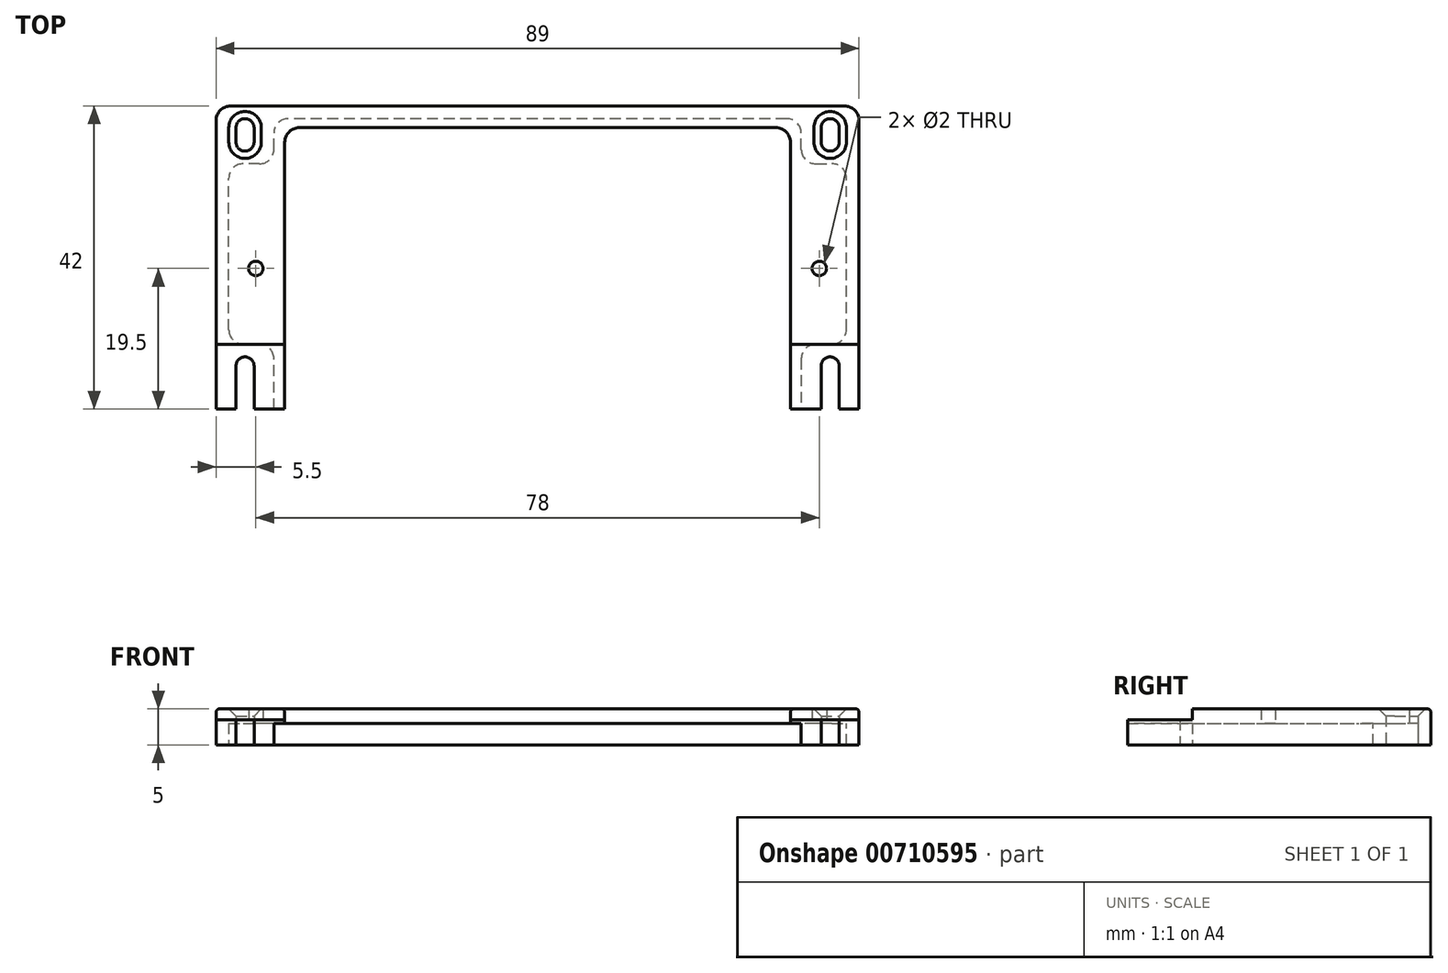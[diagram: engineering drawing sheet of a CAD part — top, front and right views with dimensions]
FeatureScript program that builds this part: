
annotation { "Feature Type Name" : "Feature", "Feature Type Description" : "" }
export const myFeature = defineFeature(function(context is Context, id is Id, definition is map)
    precondition{}
    {
        {
            var Q0;
            Q0=qCreatedBy(makeId("Top.planeOp"),FACE);
            var sketch = newSketch(context, id + "F0", { "sketchPlane" : qUnion([Q0])});
            skLineSegment(sketch, "E0.bottom", {"start": v(44.5, -22.5) * mm, "end": v(-44.5, -22.5) * mm});
            skLineSegment(sketch, "E0.top", {"start": v(44.5, 22.5) * mm, "end": v(-44.5, 22.5) * mm});
            skLineSegment(sketch, "E0.left", {"start": v(44.5, -22.5) * mm, "end": v(44.5, 22.5) * mm});
            skLineSegment(sketch, "E0.right", {"start": v(-44.5, -22.5) * mm, "end": v(-44.5, 22.5) * mm});
            skPoint(sketch, "E0.middle", {"position": v(0, 0) * mm});
            skSolve(sketch);
        }
        {
            var Q0;
            Q0=qSketchRegion(id+"F0",true);
            extrude(context, id + "F1", {"entities" : qUnion([Q0]), "depth" : 5 * mm, "offsetDistance" : 25 * mm});
        }
        {
            var Q0;
            Q0=qCreatedBy(makeId("Top.planeOp"),FACE);
            var sketch = newSketch(context, id + "F2", { "sketchPlane" : qUnion([Q0])});
            skLineSegment(sketch, "E1.bottom", {"start": v(35, -19.5) * mm, "end": v(-35, -19.5) * mm});
            skLineSegment(sketch, "E1.top", {"start": v(35, 19.5) * mm, "end": v(-35, 19.5) * mm});
            skLineSegment(sketch, "E1.left", {"start": v(35, -19.5) * mm, "end": v(35, 19.5) * mm});
            skLineSegment(sketch, "E1.right", {"start": v(-35, -19.5) * mm, "end": v(-35, 19.5) * mm});
            skPoint(sketch, "E1.middle", {"position": v(0, 0) * mm});
            skSolve(sketch);
        }
        {
            var Q0;
            Q0=qSketchRegion(id+"F2",true);
            extrude(context, id + "F3", {"entities" : qUnion([Q0]), "operationType" : NewBodyOperationType.REMOVE, "depth" : 25 * mm, "offsetDistance" : 25 * mm});
        }
        {
            var Q0;
            Q0=qCreatedBy(makeId("Top.planeOp"),FACE);
            var sketch = newSketch(context, id + "F4", { "sketchPlane" : qUnion([Q0])});
            skLineSegment(sketch, "E2.bottom", {"start": v(42.75, -20.75) * mm, "end": v(-42.75, -20.75) * mm});
            skLineSegment(sketch, "E2.top", {"start": v(42.75, 20.75) * mm, "end": v(-42.75, 20.75) * mm});
            skLineSegment(sketch, "E2.left", {"start": v(42.75, -20.75) * mm, "end": v(42.75, 20.75) * mm});
            skLineSegment(sketch, "E2.right", {"start": v(-42.75, -20.75) * mm, "end": v(-42.75, 20.75) * mm});
            skPoint(sketch, "E2.middle", {"position": v(0, 0) * mm});
            skSolve(sketch);
        }
        {
            var Q0;
            Q0=qSketchRegion(id+"F4",true);
            extrude(context, id + "F5", {"entities" : qUnion([Q0]), "operationType" : NewBodyOperationType.REMOVE, "depth" : 3 * mm, "offsetDistance" : 25 * mm});
        }
        {
            var Q0;
            Q0=qCreatedBy(makeId("Top.planeOp"),FACE);
            var sketch = newSketch(context, id + "F6", { "sketchPlane" : qUnion([Q0])});
            skLineSegment(sketch, "E3.bottom", {"start": v(-36.5, 14.5) * mm, "end": v(-44.5, 14.5) * mm});
            skLineSegment(sketch, "E3.top", {"start": v(-36.5, 22.5) * mm, "end": v(-44.5, 22.5) * mm});
            skLineSegment(sketch, "E3.left", {"start": v(-36.5, 14.5) * mm, "end": v(-36.5, 22.5) * mm});
            skLineSegment(sketch, "E3.right", {"start": v(-44.5, 14.5) * mm, "end": v(-44.5, 22.5) * mm});
            skPoint(sketch, "E3.middle", {"position": v(-40.5, 18.5) * mm});
            skLineSegment(sketch, "E4.bottom", {"start": v(-44.5, -22.5) * mm, "end": v(-36.5, -22.5) * mm});
            skLineSegment(sketch, "E4.top", {"start": v(-44.5, -10.5) * mm, "end": v(-36.5, -10.5) * mm});
            skLineSegment(sketch, "E4.left", {"start": v(-44.5, -22.5) * mm, "end": v(-44.5, -10.5) * mm});
            skLineSegment(sketch, "E4.right", {"start": v(-36.5, -22.5) * mm, "end": v(-36.5, -10.5) * mm});
            skPoint(sketch, "E4.middle", {"position": v(-40.5, -16.5) * mm});
            skLineSegment(sketch, "E5.bottom", {"start": v(36.5, 14.5) * mm, "end": v(44.5, 14.5) * mm});
            skLineSegment(sketch, "E5.top", {"start": v(36.5, 22.5) * mm, "end": v(44.5, 22.5) * mm});
            skLineSegment(sketch, "E5.left", {"start": v(36.5, 14.5) * mm, "end": v(36.5, 22.5) * mm});
            skLineSegment(sketch, "E5.right", {"start": v(44.5, 14.5) * mm, "end": v(44.5, 22.5) * mm});
            skPoint(sketch, "E5.middle", {"position": v(40.5, 18.5) * mm});
            skLineSegment(sketch, "E6.bottom", {"start": v(44.5, -10.5) * mm, "end": v(36.5, -10.5) * mm});
            skLineSegment(sketch, "E6.top", {"start": v(44.5, -22.5) * mm, "end": v(36.5, -22.5) * mm});
            skLineSegment(sketch, "E6.left", {"start": v(44.5, -10.5) * mm, "end": v(44.5, -22.5) * mm});
            skLineSegment(sketch, "E6.right", {"start": v(36.5, -10.5) * mm, "end": v(36.5, -22.5) * mm});
            skSolve(sketch);
        }
        {
            var Q0;
            Q0=qSketchRegion(id+"F6",true);
            extrude(context, id + "F7", {"entities" : qUnion([Q0]), "operationType" : NewBodyOperationType.ADD, "depth" : 3 * mm, "offsetDistance" : 25 * mm});
        }
        {
            var Q0;
            Q0=qCreatedBy(makeId("Top.planeOp"),FACE);
            var sketch = newSketch(context, id + "F8", { "sketchPlane" : qUnion([Q0])});
            skCircle(sketch, "E7", {"center": v(40.5, -13.5) * mm, "radius": 1.25 * mm});
            skCircle(sketch, "E8", {"center": v(40.5, 19.5) * mm, "radius": 1.25 * mm});
            skCircle(sketch, "E9", {"center": v(-40.5, -13.5) * mm, "radius": 1.25 * mm});
            skCircle(sketch, "E10", {"center": v(-40.5, 19.5) * mm, "radius": 1.25 * mm});
            skCircle(sketch, "E11", {"center": v(-39, 0) * mm, "radius": 1 * mm});
            skCircle(sketch, "E12", {"center": v(39, 0) * mm, "radius": 1 * mm});
            skCircle(sketch, "E13.1.0.0", {"center": v(-40.5, 17.5) * mm, "radius": 1.25 * mm});
            skLineSegment(sketch, "E13.direction1", {"start": v(-40.5, 19.5) * mm, "end": v(-40.5, 17.5) * mm, "construction": true});
            skCircle(sketch, "E14.1.0.0", {"center": v(40.5, 17.5) * mm, "radius": 1.25 * mm});
            skLineSegment(sketch, "E14.direction1", {"start": v(40.5, 19.5) * mm, "end": v(40.5, 17.5) * mm, "construction": true});
            skLineSegment(sketch, "E15.bottom", {"start": v(-41.75, -13.5) * mm, "end": v(-39.25, -13.5) * mm});
            skLineSegment(sketch, "E15.top", {"start": v(-41.75, -23.5) * mm, "end": v(-39.25, -23.5) * mm});
            skLineSegment(sketch, "E15.left", {"start": v(-41.75, -13.5) * mm, "end": v(-41.75, -23.5) * mm});
            skLineSegment(sketch, "E15.right", {"start": v(-39.25, -13.5) * mm, "end": v(-39.25, -23.5) * mm});
            skLineSegment(sketch, "E16.bottom", {"start": v(39.25, -13.5) * mm, "end": v(41.75, -13.5) * mm});
            skLineSegment(sketch, "E16.top", {"start": v(39.25, -23.5) * mm, "end": v(41.75, -23.5) * mm});
            skLineSegment(sketch, "E16.left", {"start": v(39.25, -13.5) * mm, "end": v(39.25, -23.5) * mm});
            skLineSegment(sketch, "E16.right", {"start": v(41.75, -13.5) * mm, "end": v(41.75, -23.5) * mm});
            skSolve(sketch);
        }
        {
            var Q0;
            Q0=qSketchRegion(id+"F8",true);
            extrude(context, id + "F9", {"entities" : qUnion([Q0]), "operationType" : NewBodyOperationType.REMOVE, "depth" : 25 * mm, "offsetDistance" : 25 * mm});
        }
        {
            var Q0;
            Q0 = qSketchRegion(id + "F8", true);
            extrude(context, id + "F10", {"entities" : qUnion([Q0]), "operationType" : NewBodyOperationType.REMOVE, "depth" : 25 * mm, "offsetDistance" : 25 * mm});
        }
        {
            var Q0;
            Q0=makeQuery(id+"F7.boolean.opBoolean","MERGE",FACE,{"derivedFrom":[makeQuery(id+"F1.opExtrude","CAP_FACE",FACE,{"disambiguationData":[OSD([sQuery(id+"F0.wireOp",EDGE,"E0.bottom"),sQuery(id+"F0.wireOp",EDGE,"E0.top"),sQuery(id+"F0.wireOp",EDGE,"E0.left"),sQuery(id+"F0.wireOp",EDGE,"E0.right")])],"isStart":true}),makeQuery(id+"F7.opExtrude","CAP_FACE",FACE,{"disambiguationData":[OSD([sQuery(id+"F6.wireOp",EDGE,"E3.bottom"),sQuery(id+"F6.wireOp",EDGE,"E3.top"),sQuery(id+"F6.wireOp",EDGE,"E3.left"),sQuery(id+"F6.wireOp",EDGE,"E3.right")])],"isStart":true}),makeQuery(id+"F7.opExtrude","CAP_FACE",FACE,{"disambiguationData":[OSD([sQuery(id+"F6.wireOp",EDGE,"E4.bottom"),sQuery(id+"F6.wireOp",EDGE,"E4.top"),sQuery(id+"F6.wireOp",EDGE,"E4.left"),sQuery(id+"F6.wireOp",EDGE,"E4.right")])],"isStart":true}),makeQuery(id+"F7.opExtrude","CAP_FACE",FACE,{"disambiguationData":[OSD([sQuery(id+"F6.wireOp",EDGE,"E5.bottom"),sQuery(id+"F6.wireOp",EDGE,"E5.top"),sQuery(id+"F6.wireOp",EDGE,"E5.left"),sQuery(id+"F6.wireOp",EDGE,"E5.right")])],"isStart":true}),makeQuery(id+"F7.opExtrude","CAP_FACE",FACE,{"disambiguationData":[OSD([sQuery(id+"F6.wireOp",EDGE,"E6.bottom"),sQuery(id+"F6.wireOp",EDGE,"E6.top"),sQuery(id+"F6.wireOp",EDGE,"E6.left"),sQuery(id+"F6.wireOp",EDGE,"E6.right")])],"isStart":true})]});
            var sketch = newSketch(context, id + "F11", { "sketchPlane" : qUnion([Q0])});
            skLineSegment(sketch, "E17.bottom", {"start": v(-41.75, -19.5) * mm, "end": v(-39.25, -19.5) * mm});
            skLineSegment(sketch, "E17.top", {"start": v(-41.75, -17.5) * mm, "end": v(-39.25, -17.5) * mm});
            skLineSegment(sketch, "E17.left", {"start": v(-41.75, -19.5) * mm, "end": v(-41.75, -17.5) * mm});
            skLineSegment(sketch, "E17.right", {"start": v(-39.25, -19.5) * mm, "end": v(-39.25, -17.5) * mm});
            skLineSegment(sketch, "E18.bottom", {"start": v(39.25, -19.5) * mm, "end": v(41.75, -19.5) * mm});
            skLineSegment(sketch, "E18.top", {"start": v(39.25, -17.5) * mm, "end": v(41.75, -17.5) * mm});
            skLineSegment(sketch, "E18.left", {"start": v(39.25, -19.5) * mm, "end": v(39.25, -17.5) * mm});
            skLineSegment(sketch, "E18.right", {"start": v(41.75, -19.5) * mm, "end": v(41.75, -17.5) * mm});
            skSolve(sketch);
        }
        {
            var Q0;
            Q0 = qSketchRegion(id + "F11", true);
            extrude(context, id + "F12", {"entities" : qUnion([Q0]), "operationType" : NewBodyOperationType.REMOVE, "oppositeDirection" : true, "depth" : 25 * mm, "offsetDistance" : 25 * mm});
        }
        {
            var Q0;
            Q0=makeQuery(id+"F1.opExtrude","CAP_FACE",FACE,{"disambiguationData":[OSD([sQuery(id+"F0.wireOp",EDGE,"E0.bottom"),sQuery(id+"F0.wireOp",EDGE,"E0.top"),sQuery(id+"F0.wireOp",EDGE,"E0.left"),sQuery(id+"F0.wireOp",EDGE,"E0.right")])],"isStart":false});
            var sketch = newSketch(context, id + "F13", { "sketchPlane" : qUnion([Q0])});
            skLineSegment(sketch, "E19.bottom", {"start": v(44.5, -22.5) * mm, "end": v(-44.5, -22.5) * mm});
            skLineSegment(sketch, "E19.top", {"start": v(44.5, -19.5) * mm, "end": v(-44.5, -19.5) * mm});
            skLineSegment(sketch, "E19.left", {"start": v(44.5, -22.5) * mm, "end": v(44.5, -19.5) * mm});
            skLineSegment(sketch, "E19.right", {"start": v(-44.5, -22.5) * mm, "end": v(-44.5, -19.5) * mm});
            skSolve(sketch);
        }
        {
            var Q0;
            Q0 = qSketchRegion(id + "F13", true);
            extrude(context, id + "F14", {"entities" : qUnion([Q0]), "operationType" : NewBodyOperationType.REMOVE, "oppositeDirection" : true, "depth" : 25 * mm, "offsetDistance" : 25 * mm});
        }
        {
            var Q0;
            Q0=makeQuery(id+"F1.opExtrude","CAP_FACE",FACE,{"disambiguationData":[OSD([sQuery(id+"F0.wireOp",EDGE,"E0.bottom"),sQuery(id+"F0.wireOp",EDGE,"E0.top"),sQuery(id+"F0.wireOp",EDGE,"E0.left"),sQuery(id+"F0.wireOp",EDGE,"E0.right")])],"isStart":false});
            var sketch = newSketch(context, id + "F15", { "sketchPlane" : qUnion([Q0])});
            skLineSegment(sketch, "E20.bottom", {"start": v(-44.5, -19.5) * mm, "end": v(44.5, -19.5) * mm});
            skLineSegment(sketch, "E20.top", {"start": v(-44.5, -10.5) * mm, "end": v(44.5, -10.5) * mm});
            skLineSegment(sketch, "E20.left", {"start": v(-44.5, -19.5) * mm, "end": v(-44.5, -10.5) * mm});
            skLineSegment(sketch, "E20.right", {"start": v(44.5, -19.5) * mm, "end": v(44.5, -10.5) * mm});
            skSolve(sketch);
        }
        {
            var Q0;
            Q0 = qSketchRegion(id + "F15", true);
            extrude(context, id + "F16", {"entities" : qUnion([Q0]), "operationType" : NewBodyOperationType.REMOVE, "oppositeDirection" : true, "depth" : 1.5 * mm, "offsetDistance" : 25 * mm});
        }
        {
            var Q0;
            Q0=makeQuery(id+"F12.boolean.opBoolean","INTERSECT",EDGE,{"derivedFrom":[makeQuery(id+"F1.opExtrude","CAP_FACE",FACE,{"disambiguationData":[OSD([sQuery(id+"F0.wireOp",EDGE,"E0.bottom"),sQuery(id+"F0.wireOp",EDGE,"E0.top"),sQuery(id+"F0.wireOp",EDGE,"E0.left"),sQuery(id+"F0.wireOp",EDGE,"E0.right")])],"isStart":false}),makeQuery(id+"F12.opExtrude","SWEPT_FACE",FACE,{"disambiguationData":[OSD([sQuery(id+"F11.wireOp",EDGE,"E18.right")])]})]});
            chamfer(context, id + "F17", {"entities" : qUnion([Q0]), "width" : 1 * mm, "tangentPropagation" : true});
        }
        {
            var Q0;
            Q0=makeQuery(id+"F12.boolean.opBoolean","INTERSECT",EDGE,{"derivedFrom":[makeQuery(id+"F1.opExtrude","CAP_FACE",FACE,{"disambiguationData":[OSD([sQuery(id+"F0.wireOp",EDGE,"E0.bottom"),sQuery(id+"F0.wireOp",EDGE,"E0.top"),sQuery(id+"F0.wireOp",EDGE,"E0.left"),sQuery(id+"F0.wireOp",EDGE,"E0.right")])],"isStart":false}),makeQuery(id+"F12.opExtrude","SWEPT_FACE",FACE,{"disambiguationData":[OSD([sQuery(id+"F11.wireOp",EDGE,"E17.right")])]})]});
            chamfer(context, id + "F18", {"entities" : qUnion([Q0]), "width" : 1 * mm, "tangentPropagation" : true});
        }
        {
            var Q0;
            Q0=makeQuery(id+"F1.opExtrude","SWEPT_EDGE",EDGE,{"disambiguationData":[OSD([sQuery(id+"F0.wireOp",EDGE,"E0.top"),sQuery(id+"F0.wireOp",EDGE,"E0.right")])]});
            var Q1;
            Q1=makeQuery(id+"F1.opExtrude","SWEPT_EDGE",EDGE,{"disambiguationData":[OSD([sQuery(id+"F0.wireOp",EDGE,"E0.top"),sQuery(id+"F0.wireOp",EDGE,"E0.left")])]});
            var Q2;
            Q2=makeQuery(id+"F3.boolean.opBoolean","COPY",EDGE,{"derivedFrom":makeQuery(id+"F3.opExtrude","SWEPT_EDGE",EDGE,{"disambiguationData":[OSD([sQuery(id+"F2.wireOp",EDGE,"E1.top"),sQuery(id+"F2.wireOp",EDGE,"E1.left")])]})});
            var Q3;
            Q3=makeQuery(id+"F3.boolean.opBoolean","COPY",EDGE,{"derivedFrom":makeQuery(id+"F3.opExtrude","SWEPT_EDGE",EDGE,{"disambiguationData":[OSD([sQuery(id+"F2.wireOp",EDGE,"E1.top"),sQuery(id+"F2.wireOp",EDGE,"E1.right")])]})});
            var Q4;
            Q4=makeQuery(id+"F7.opExtrude","SWEPT_EDGE",EDGE,{"disambiguationData":[OSD([sQuery(id+"F6.wireOp",EDGE,"E3.bottom"),sQuery(id+"F6.wireOp",EDGE,"E3.left")])]});
            var Q5;
            Q5=makeQuery(id+"F7.boolean.opBoolean","INTERSECT",EDGE,{"derivedFrom":[makeQuery(id+"F5.boolean.opBoolean","COPY",FACE,{"derivedFrom":makeQuery(id+"F5.opExtrude","SWEPT_FACE",FACE,{"disambiguationData":[OSD([sQuery(id+"F4.wireOp",EDGE,"E2.top")])]})}),makeQuery(id+"F7.opExtrude","SWEPT_FACE",FACE,{"disambiguationData":[OSD([sQuery(id+"F6.wireOp",EDGE,"E3.left")])]})]});
            var Q6;
            Q6=makeQuery(id+"F7.boolean.opBoolean","INTERSECT",EDGE,{"derivedFrom":[makeQuery(id+"F5.boolean.opBoolean","COPY",FACE,{"derivedFrom":makeQuery(id+"F5.opExtrude","SWEPT_FACE",FACE,{"disambiguationData":[OSD([sQuery(id+"F4.wireOp",EDGE,"E2.right")])]})}),makeQuery(id+"F7.opExtrude","SWEPT_FACE",FACE,{"disambiguationData":[OSD([sQuery(id+"F6.wireOp",EDGE,"E3.bottom")])]})]});
            var Q7;
            Q7=makeQuery(id+"F7.boolean.opBoolean","INTERSECT",EDGE,{"derivedFrom":[makeQuery(id+"F5.boolean.opBoolean","COPY",FACE,{"derivedFrom":makeQuery(id+"F5.opExtrude","SWEPT_FACE",FACE,{"disambiguationData":[OSD([sQuery(id+"F4.wireOp",EDGE,"E2.right")])]})}),makeQuery(id+"F7.opExtrude","SWEPT_FACE",FACE,{"disambiguationData":[OSD([sQuery(id+"F6.wireOp",EDGE,"E4.top")])]})]});
            var Q8;
            Q8=makeQuery(id+"F7.opExtrude","SWEPT_EDGE",EDGE,{"disambiguationData":[OSD([sQuery(id+"F6.wireOp",EDGE,"E4.top"),sQuery(id+"F6.wireOp",EDGE,"E4.right")])]});
            var Q9;
            Q9=makeQuery(id+"F7.boolean.opBoolean","INTERSECT",EDGE,{"derivedFrom":[makeQuery(id+"F5.boolean.opBoolean","COPY",FACE,{"derivedFrom":makeQuery(id+"F5.opExtrude","SWEPT_FACE",FACE,{"disambiguationData":[OSD([sQuery(id+"F4.wireOp",EDGE,"E2.top")])]})}),makeQuery(id+"F7.opExtrude","SWEPT_FACE",FACE,{"disambiguationData":[OSD([sQuery(id+"F6.wireOp",EDGE,"E5.left")])]})]});
            var Q10;
            Q10=makeQuery(id+"F7.opExtrude","SWEPT_EDGE",EDGE,{"disambiguationData":[OSD([sQuery(id+"F6.wireOp",EDGE,"E5.bottom"),sQuery(id+"F6.wireOp",EDGE,"E5.left")])]});
            var Q11;
            Q11=makeQuery(id+"F7.boolean.opBoolean","INTERSECT",EDGE,{"derivedFrom":[makeQuery(id+"F5.boolean.opBoolean","COPY",FACE,{"derivedFrom":makeQuery(id+"F5.opExtrude","SWEPT_FACE",FACE,{"disambiguationData":[OSD([sQuery(id+"F4.wireOp",EDGE,"E2.left")])]})}),makeQuery(id+"F7.opExtrude","SWEPT_FACE",FACE,{"disambiguationData":[OSD([sQuery(id+"F6.wireOp",EDGE,"E5.bottom")])]})]});
            var Q12;
            Q12=makeQuery(id+"F7.boolean.opBoolean","INTERSECT",EDGE,{"derivedFrom":[makeQuery(id+"F5.boolean.opBoolean","COPY",FACE,{"derivedFrom":makeQuery(id+"F5.opExtrude","SWEPT_FACE",FACE,{"disambiguationData":[OSD([sQuery(id+"F4.wireOp",EDGE,"E2.left")])]})}),makeQuery(id+"F7.opExtrude","SWEPT_FACE",FACE,{"disambiguationData":[OSD([sQuery(id+"F6.wireOp",EDGE,"E6.bottom")])]})]});
            var Q13;
            Q13=makeQuery(id+"F7.opExtrude","SWEPT_EDGE",EDGE,{"disambiguationData":[OSD([sQuery(id+"F6.wireOp",EDGE,"E6.bottom"),sQuery(id+"F6.wireOp",EDGE,"E6.right")])]});
            fillet(context, id + "F19", {"entities" : qUnion([Q0, Q1, Q2, Q3, Q4, Q5, Q6, Q7, Q8, Q9, Q10, Q11, Q12, Q13]), "radius" : 2 * mm, "tangentPropagation" : true, "allowEdgeOverflow" : false});
        }
        {
            var Q0;
            Q0=makeQuery(id+"F1.opExtrude","CAP_EDGE",EDGE,{"disambiguationData":[OSD([sQuery(id+"F0.wireOp",EDGE,"E0.top")])],"isStart":false});
            var Q1;
            {var subQ0=sQuery(id+"F0.wireOp",EDGE,"E0.right");var subQ1=sQuery(id+"F15.wireOp",EDGE,"E20.top");Q1=makeQuery(id+"F16.boolean.opBoolean","COPY",EDGE,{"disambiguationData":[TD([makeQuery(id+"F1.opExtrude","SWEPT_FACE",FACE,{"disambiguationData":[OSD([subQ0])]})])],"derivedFrom":makeQuery(id+"F16.opExtrude","CAP_EDGE",EDGE,{"disambiguationData":[OSD([subQ1])],"isStart":true})});}
            var Q2;
            {var subQ0=sQuery(id+"F0.wireOp",EDGE,"E0.left");var subQ1=sQuery(id+"F15.wireOp",EDGE,"E20.top");Q2=makeQuery(id+"F16.boolean.opBoolean","COPY",EDGE,{"disambiguationData":[TD([makeQuery(id+"F1.opExtrude","SWEPT_FACE",FACE,{"disambiguationData":[OSD([subQ0])]})])],"derivedFrom":makeQuery(id+"F16.opExtrude","CAP_EDGE",EDGE,{"disambiguationData":[OSD([subQ1])],"isStart":true})});}
            var Q3;
            Q3=makeQuery(id+"F3.boolean.opBoolean","INTERSECT",EDGE,{"derivedFrom":[makeQuery(id+"F1.opExtrude","CAP_FACE",FACE,{"disambiguationData":[OSD([sQuery(id+"F0.wireOp",EDGE,"E0.bottom"),sQuery(id+"F0.wireOp",EDGE,"E0.top"),sQuery(id+"F0.wireOp",EDGE,"E0.left"),sQuery(id+"F0.wireOp",EDGE,"E0.right")])],"isStart":false}),makeQuery(id+"F3.opExtrude","SWEPT_FACE",FACE,{"disambiguationData":[OSD([sQuery(id+"F2.wireOp",EDGE,"E1.left")])]})]});
            fillet(context, id + "F20", {"entities" : qUnion([Q0, Q1, Q2, Q3]), "radius" : 0.5 * mm, "tangentPropagation" : true, "allowEdgeOverflow" : false});
        }
    });
